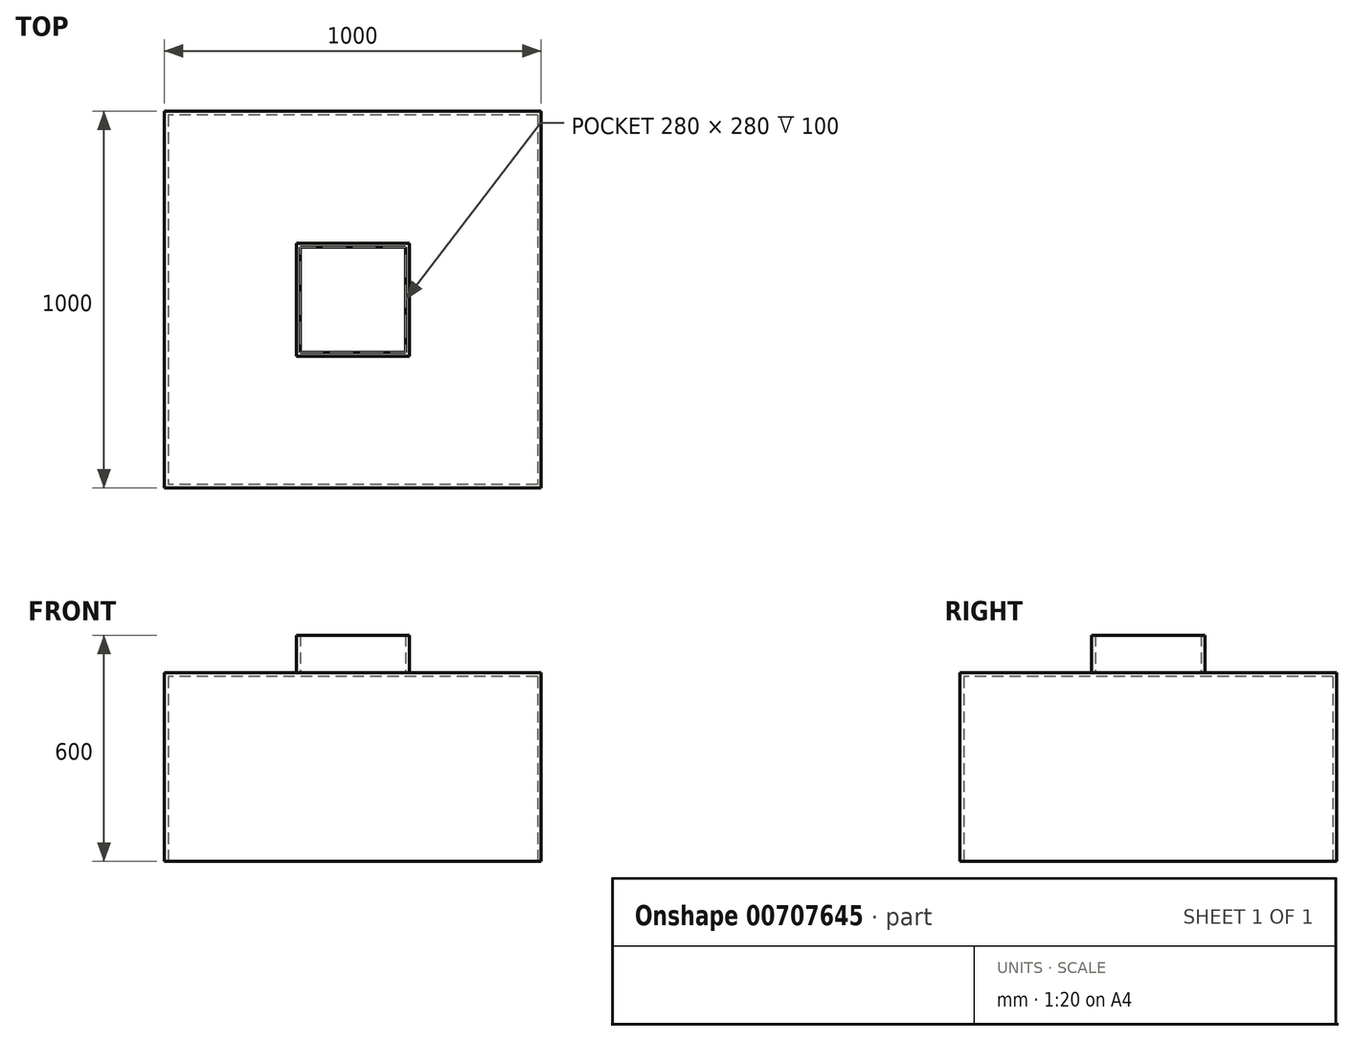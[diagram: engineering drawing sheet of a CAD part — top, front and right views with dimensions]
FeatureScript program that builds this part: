
annotation { "Feature Type Name" : "Feature", "Feature Type Description" : "" }
export const myFeature = defineFeature(function(context is Context, id is Id, definition is map)
    precondition{}
    {
        {
            var Q0;
            Q0=qCreatedBy(makeId("Top.planeOp"),FACE);
            var sketch = newSketch(context, id + "F0", { "sketchPlane" : qUnion([Q0])});
            skLineSegment(sketch, "E0.bottom", {"start": v(500, 500) * mm, "end": v(-500, 500) * mm});
            skLineSegment(sketch, "E0.top", {"start": v(500, -500) * mm, "end": v(-500, -500) * mm});
            skLineSegment(sketch, "E0.left", {"start": v(500, 500) * mm, "end": v(500, -500) * mm});
            skLineSegment(sketch, "E0.right", {"start": v(-500, 500) * mm, "end": v(-500, -500) * mm});
            skPoint(sketch, "E0.middle", {"position": v(0, 0) * mm});
            skSolve(sketch);
        }
        {
            var Q0;
            Q0=makeQuery(id+"F0.imprint","IMPRINT",FACE,{"disambiguationData":[TD([[makeQuery(id+"F0.imprint","IMPRINT",EDGE,{"derivedFrom":sQuery(id+"F0.wireOp",EDGE,"E0.bottom")}),1.0]])]});
            extrude(context, id + "F1", {"entities" : qUnion([Q0]), "depth" : 500 * mm, "offsetDistance" : 25 * mm});
        }
        {
            var Q0;
            Q0=makeQuery(id+"F1.opExtrude","CAP_FACE",FACE,{"disambiguationData":[OSD([sQuery(id+"F0.wireOp",EDGE,"E0.bottom"),sQuery(id+"F0.wireOp",EDGE,"E0.top"),sQuery(id+"F0.wireOp",EDGE,"E0.left"),sQuery(id+"F0.wireOp",EDGE,"E0.right")])],"isStart":false});
            var sketch = newSketch(context, id + "F2", { "sketchPlane" : qUnion([Q0])});
            skLineSegment(sketch, "E1.bottom", {"start": v(150, 150) * mm, "end": v(-150, 150) * mm});
            skLineSegment(sketch, "E1.top", {"start": v(150, -150) * mm, "end": v(-150, -150) * mm});
            skLineSegment(sketch, "E1.left", {"start": v(150, 150) * mm, "end": v(150, -150) * mm});
            skLineSegment(sketch, "E1.right", {"start": v(-150, 150) * mm, "end": v(-150, -150) * mm});
            skPoint(sketch, "E1.middle", {"position": v(0, 0) * mm});
            skSolve(sketch);
        }
        {
            var Q0;
            Q0=makeQuery(id+"F1.opExtrude","CAP_FACE",FACE,{"disambiguationData":[OSD([sQuery(id+"F0.wireOp",EDGE,"E0.bottom"),sQuery(id+"F0.wireOp",EDGE,"E0.top"),sQuery(id+"F0.wireOp",EDGE,"E0.left"),sQuery(id+"F0.wireOp",EDGE,"E0.right")])],"isStart":true});
            shell(context, id + "F3", {"entities" : qUnion([Q0]), "thickness" : 10 * mm});
        }
        {
            var Q0;
            Q0=makeQuery(id+"F2.imprint","IMPRINT",FACE,{"disambiguationData":[TD([[makeQuery(id+"F2.imprint","IMPRINT",EDGE,{"derivedFrom":sQuery(id+"F2.wireOp",EDGE,"E1.bottom")}),1.0]])]});
            extrude(context, id + "F4", {"entities" : qUnion([Q0]), "operationType" : NewBodyOperationType.ADD, "depth" : 100 * mm, "offsetDistance" : 25 * mm});
        }
        {
            var Q0;
            Q0=makeQuery(id+"F4.opExtrude","CAP_FACE",FACE,{"disambiguationData":[OSD([sQuery(id+"F2.wireOp",EDGE,"E1.bottom"),sQuery(id+"F2.wireOp",EDGE,"E1.top"),sQuery(id+"F2.wireOp",EDGE,"E1.left"),sQuery(id+"F2.wireOp",EDGE,"E1.right")])],"isStart":false});
            shell(context, id + "F5", {"entities" : qUnion([Q0]), "thickness" : 10 * mm});
        }
    });
